FCSTD DOCUMENT  (FreeCAD 0.21R33694 (Git))
Label: lid_assembly
License: All rights reserved
LicenseURL: http://en.wikipedia.org/wiki/All_rights_reserved
objects: App::Link×9, App::Part×1
EXTERNAL_REF file=../master_kumiko_box.FCStd obj=Spreadsheet
EXTERNAL_REF file=../parts/box/kumiko_lid_long.FCStd obj=Body001
EXTERNAL_REF file=../parts/box/kumiko_lid_short.FCStd obj=Body001
EXTERNAL_REF file=../parts/box/kumiko_box_key_miter.FCStd obj=Body014

FEATURE [App::Link] Link  label="SpreadSheet"
  LinkedObject = -> <external ../master_kumiko_box.FCStd>#Spreadsheet
FEATURE [App::Link] Link001  label="lid_front"
  LinkPlacement = pos=(0,0,0) rot=(0,0,1;1.5708rad)
  LinkedObject = -> <external ../parts/box/kumiko_lid_long.FCStd>#Body001
  Placement = pos=(0,0,0) rot=(0,0,1;1.5708rad)
  expr: .Placement.Base.x = 0
FEATURE [App::Link] Link002  label="lid_left"
  LinkPlacement = pos=(0,75,0) rot=(0,0,1;0rad)
  LinkedObject = -> <external ../parts/box/kumiko_lid_short.FCStd>#Body001
  Placement = pos=(0,75,0) rot=(0,0,1;0rad)
  expr: .Placement.Base.y = <<SpreadSheet>>.box_width
FEATURE [App::Link] Link003  label="lid_back"
  LinkPlacement = pos=(130,75,0) rot=(0,0,1;4.71239rad)
  LinkedObject = -> <external ../parts/box/kumiko_lid_long.FCStd>#Body001
  Placement = pos=(130,75,0) rot=(0,0,1;4.71239rad)
  expr: .Placement.Base.x = <<SpreadSheet>>.box_length
  expr: .Placement.Base.y = <<SpreadSheet>>.box_width
FEATURE [App::Link] Link004  label="lid_side"
  LinkPlacement = pos=(130,0,0) rot=(0,0,1;3.14159rad)
  LinkedObject = -> <external ../parts/box/kumiko_lid_short.FCStd>#Body001
  Placement = pos=(130,0,0) rot=(0,0,1;3.14159rad)
  expr: .Placement.Base.x = <<SpreadSheet>>.box_length
  expr: .Placement.Rotation.Angle = 180
FEATURE [App::Link] Link005  label="miter_key_a"
  LinkPlacement = pos=(0,0,7) rot=(0,0,1;0rad)
  LinkedObject = -> <external ../parts/box/kumiko_box_key_miter.FCStd>#Body014
  Placement = pos=(0,0,7) rot=(0,0,1;0rad)
  expr: .Placement.Base.z = (<<SpreadSheet>>.lid_height - <<SpreadSheet>>.kumiko_thickness) / 2
FEATURE [App::Link] Link006  label="miter_key_b"
  LinkPlacement = pos=(130,0,7) rot=(0,0,1;1.5708rad)
  LinkedObject = -> <external ../parts/box/kumiko_box_key_miter.FCStd>#Body014
  Placement = pos=(130,0,7) rot=(0,0,1;1.5708rad)
  expr: .Placement.Base.x = <<SpreadSheet>>.box_length
  expr: .Placement.Base.z = (<<SpreadSheet>>.lid_height - <<SpreadSheet>>.kumiko_thickness) / 2
  expr: .Placement.Rotation.Angle = 90
FEATURE [App::Link] Link007  label="miter_key_c"
  LinkPlacement = pos=(130,75,7) rot=(0,0,1;3.14159rad)
  LinkedObject = -> <external ../parts/box/kumiko_box_key_miter.FCStd>#Body014
  Placement = pos=(130,75,7) rot=(0,0,1;3.14159rad)
  expr: .Placement.Base.x = <<SpreadSheet>>.box_length
  expr: .Placement.Base.y = <<SpreadSheet>>.box_width
  expr: .Placement.Base.z = (<<SpreadSheet>>.lid_height - <<SpreadSheet>>.kumiko_thickness) / 2
FEATURE [App::Link] Link008  label="miter_key_d"
  LinkPlacement = pos=(0,75,7) rot=(0,0,1;4.71239rad)
  LinkedObject = -> <external ../parts/box/kumiko_box_key_miter.FCStd>#Body014
  Placement = pos=(0,75,7) rot=(0,0,1;4.71239rad)
  expr: .Placement.Base.y = <<SpreadSheet>>.box_width
  expr: .Placement.Base.z = (<<SpreadSheet>>.lid_height - <<SpreadSheet>>.kumiko_thickness) / 2
  expr: .Placement.Rotation.Angle = 270
FEATURE [App::Part] Part  label="lid"
  Group = -> [Link004,Link003,Link002,Link001,Link005,Link006,Link007,Link008]
  Origin = -> Origin

RESOLVED EXTERNAL PARTS (link-assembly join: the EXTERNAL_REF files above that resolve inside this repo's crawl, each included once):
---- part ../master_kumiko_box.FCStd = doc fcstd_d57fc246fb5e ----
FCSTD DOCUMENT  (FreeCAD 0.21R33771 (Git))
Label: master_kumiko_box
License: All rights reserved
LicenseURL: https://en.wikipedia.org/wiki/All_rights_reserved
objects: App::Link×3, App::Part×2, Spreadsheet::Sheet×1
EXTERNAL_REF file=assembly/box_assembly.FCStd obj=Part
EXTERNAL_REF file=assembly/lid_assembly.FCStd obj=Part
EXTERNAL_REF file=assembly/kumiko_assembly.FCStd obj=Part001

FEATURE [Spreadsheet::Sheet] Spreadsheet  label="SpreadSheet"
  cells = A1='name; B1='value; C1='calc (y/n); A2='box_length; B2(box_length)=130; C2='n; A3='box_width; B3(box_width)==B2 / 2 + B5 - B13 / 2; C3='n; A4='box_height; B4(box_height)=60; C4='y; A5='box_thickness; B5(box_thickness)=11.5; C5='y; A7='lid_height; B7(lid_height)==B8 * 17 / 8.5; C7='y; A8='lid_frame_width; B8(lid_frame_width)==B5 - B13; C8='y; A9='lid_lip_width; B9(lid_lip_width)==B5 - B8; C9='y; A10='lid_lip_height; B10(lid_lip_hight)=3; C10='y; A12='kumiko_hight; B12(kumiko_hight)==B7 * 11 / 17; C12='y; A13='kumiko_thickness; B13(kumiko_thickness)=3; C13='n; A14='kumiko_grid_size; B14(kumiko_grid_size)==(B2 - 2 * B8 - B13) / 4; C14='y; A16='box_wall_height; B16(box_wall_height)==B4 - B7 - B18; C16='y; A18='floor_edge; B18(floor_edge)=2; C18='n; A20='cnc_spacing; B20(cnc_spacing)=0; C20='y
FEATURE [App::Link] Link  label="box"
  LinkedObject = -> <external assembly/box_assembly.FCStd>#Part
FEATURE [App::Link] Link001  label="lid"
  LinkPlacement = pos=(0,0,43) rot=(0,0,1;0rad)
  LinkedObject = -> <external assembly/lid_assembly.FCStd>#Part
  Placement = pos=(0,0,43) rot=(0,0,1;0rad)
  expr: .Placement.Base.z = <<SpreadSheet>>.box_height - <<SpreadSheet>>.lid_height
FEATURE [App::Link] Link002  label="kumiko_assembly"
  LinkPlacement = pos=(8.5,8.5,49) rot=(0,0,1;0rad)
  LinkedObject = -> <external assembly/kumiko_assembly.FCStd>#Part001
  Placement = pos=(8.5,8.5,49) rot=(0,0,1;0rad)
  expr: .Placement.Base.x = <<SpreadSheet>>.lid_frame_width
  expr: .Placement.Base.y = <<SpreadSheet>>.lid_frame_width
  expr: .Placement.Base.z = <<SpreadSheet>>.box_height - Spreadsheet.kumiko_hight
FEATURE [App::Part] Part  label="lid_complete"
  Group = -> [Link002,Link001]
  Origin = -> Origin
FEATURE [App::Part] Part001  label="kumiko_box_complete"
  Group = -> [Part,Link]
  Origin = -> Origin001
---- part ../parts/box/kumiko_box_key_miter.FCStd = doc fcstd_dc4a3549b709 ----
FCSTD DOCUMENT  (FreeCAD 0.21R33694 (Git))
Label: kumiko_box_key_miter
License: All rights reserved
LicenseURL: https://en.wikipedia.org/wiki/All_rights_reserved
objects: Sketcher::SketchObject×1, PartDesign::Pad×1, PartDesign::Body×1, App::Link×1
note: 4 computed .brp shape members not serialized (recipe doc carries the construction recipe); baked Part::Feature solids carry a one-line shape summary decoded from their .brp
EXTERNAL_REF file=../../master_kumiko_box.FCStd obj=Spreadsheet

FEATURE [Sketcher::SketchObject] Sketch027  label="miter_key_drawing"
  FullyConstrained = true
  MapMode = 5
  Support = -> [XY_Plane016]
  expr: Constraints[6] = <<SpreadSheet>>.lid_frame_width
  expr: Constraints[7] = 0
  expr: Constraints[8] = 0
  sketch-geometry (3):
    g0: LineSegment StartX=0 StartY=8.5 StartZ=0 EndX=0 EndY=0 EndZ=0
    g1: LineSegment StartX=0 StartY=0 StartZ=0 EndX=8.5 EndY=0 EndZ=0
    g2: LineSegment StartX=8.5 StartY=0 StartZ=0 EndX=0 EndY=8.5 EndZ=0
  constraints (9):
    c: Vertical(g0)
    c: Coincident(g1,g0)
    c: Horizontal(g1)
    c: Coincident(g2,g1)
    c: Coincident(g2,g0)
    c: Equal(g0,g1)
    c: DistanceX(g1,g1) = 8.5
    c: DistanceX(g-1,g0) = 0
    c: DistanceY(g0,g-1) = 0
FEATURE [PartDesign::Pad] Pad012  label="miter_key_extrude"
  Direction = (0,0,1)
  Length = 3
  Length2 = 10
  Profile = -> Sketch027
  ReferenceAxis = -> Sketch027 [N_Axis]
  Type = 0
  expr: Length = <<SpreadSheet>>.kumiko_thickness
FEATURE [PartDesign::Body] Body014  label="miter_key"
  Group = -> [Sketch027,Pad012]
  Origin = -> Origin016
  Tip = -> Pad012
  expr: .Placement.Base.x = 0
  expr: .Placement.Base.y = 0
  expr: .Placement.Base.z = 0
  expr: .Placement.Rotation.Angle = 0
  expr: .Placement.Rotation.Axis.x = 0
  expr: .Placement.Rotation.Axis.y = 0
  expr: .Placement.Rotation.Axis.z = 1
FEATURE [App::Link] Link  label="SpreadSheet"
  LinkedObject = -> <external ../../master_kumiko_box.FCStd>#Spreadsheet
---- part ../parts/box/kumiko_lid_long.FCStd = doc fcstd_c46aa1aee5ec ----
FCSTD DOCUMENT  (FreeCAD 0.21R33694 (Git))
Label: kumiko_lid_long
License: All rights reserved
LicenseURL: https://en.wikipedia.org/wiki/All_rights_reserved
objects: Sketcher::SketchObject×3, PartDesign::Pocket×2, PartDesign::Pad×1, PartDesign::Mirrored×1, PartDesign::Body×1, App::Link×1
note: 11 computed .brp shape members not serialized (recipe doc carries the construction recipe); baked Part::Feature solids carry a one-line shape summary decoded from their .brp
EXTERNAL_REF file=../../master_kumiko_box.FCStd obj=Spreadsheet

FEATURE [Sketcher::SketchObject] Sketch004  label="lid_profile_drawing"
  FullyConstrained = true
  MapMode = 5
  Placement = pos=(0,0,0) rot=(1,0,0;1.5708rad)
  Support = -> [XZ_Plane001]
  expr: Constraints[18] = <<SpreadSheet>>.lid_height
  expr: Constraints[19] = <<SpreadSheet>>.kumiko_hight
  expr: Constraints[20] = <<SpreadSheet>>.lid_lip_hight
  expr: Constraints[21] = <<SpreadSheet>>.lid_frame_width
  expr: Constraints[22] = <<SpreadSheet>>.box_thickness / 2
  expr: Constraints[23] = <<SpreadSheet>>.box_thickness
  sketch-geometry (8):
    g0: LineSegment StartX=0 StartY=0 StartZ=0 EndX=0 EndY=17 EndZ=0
    g1: LineSegment StartX=0 StartY=17 StartZ=0 EndX=8.5 EndY=17 EndZ=0
    g2: LineSegment StartX=8.5 StartY=17 StartZ=0 EndX=8.5 EndY=6 EndZ=0
    g3: LineSegment StartX=8.5 StartY=6 StartZ=0 EndX=11.5 EndY=6 EndZ=0
    g4: LineSegment StartX=11.5 StartY=6 StartZ=0 EndX=11.5 EndY=3 EndZ=0
    g5: LineSegment StartX=11.5 StartY=3 StartZ=0 EndX=5.75 EndY=3 EndZ=0
    g6: LineSegment StartX=5.75 StartY=3 StartZ=0 EndX=5.75 EndY=0 EndZ=0
    g7: LineSegment StartX=5.75 StartY=0 StartZ=0 EndX=0 EndY=0 EndZ=0
  constraints (24):
    c: Vertical(g0)
    c: Coincident(g1,g0)
    c: Horizontal(g1)
    c: Coincident(g2,g1)
    c: Vertical(g2)
    c: Coincident(g3,g2)
    c: Horizontal(g3)
    c: Coincident(g4,g3)
    c: Vertical(g4)
    c: Coincident(g5,g4)
    c: Horizontal(g5)
    c: Coincident(g6,g5)
    c: Vertical(g6)
    c: Coincident(g7,g6)
    c: Coincident(g7,g0)
    c: Horizontal(g7)
    c: DistanceX(g-1,g0) = 0
    c: DistanceY(g-1,g0) = 0
    c: DistanceY(g0,g0) = 17
    c: DistanceY(g2,g2) = 11
    c: DistanceY(g4,g4) = 3
    c: DistanceX(g1,g1) = 8.5
    c: DistanceX(g5,g5) = 5.75
    c: DistanceX(g0,g3) = 11.5
FEATURE [PartDesign::Pad] Pad001  label="lid_extrusion"
  Direction = (0,-1,-2e-16)
  Length = 65
  Length2 = 10
  Placement = pos=(0,0,0) rot=(1,0,0;1.5708rad)
  Profile = -> Sketch004
  ReferenceAxis = -> Sketch004 [N_Axis]
  Type = 0
  expr: Length = <<SpreadSheet>>.box_length / 2
FEATURE [Sketcher::SketchObject] Sketch005  label="miter_drawing"
  FullyConstrained = true
  MapMode = 5
  Placement = pos=(0,0,0) rot=(1,0,0;3.14159rad)
  Support = -> [Pad001]
  expr: Constraints[6] = <<SpreadSheet>>.box_thickness
  expr: Constraints[8] = <<SpreadSheet>>.box_thickness
  sketch-geometry (3):
    g0: LineSegment StartX=0 StartY=0 StartZ=0 EndX=11.5 EndY=0 EndZ=0
    g1: LineSegment StartX=11.5 StartY=0 StartZ=0 EndX=11.5 EndY=11.5 EndZ=0
    g2: LineSegment StartX=11.5 StartY=11.5 StartZ=0 EndX=0 EndY=0 EndZ=0
  constraints (9):
    c: Horizontal(g0)
    c: Coincident(g1,g0)
    c: Vertical(g1)
    c: Coincident(g2,g1)
    c: Coincident(g2,g0)
    c: DistanceX(g-1,g0) = 0
    c: DistanceX(g-1,g0) = 11.5
    c: DistanceY(g0,g-1) = 0
    c: DistanceY(g0,g1) = 11.5
FEATURE [PartDesign::Pocket] Pocket002  label="miter_cut"
  BaseFeature = -> Pad001
  Direction = (0,-2e-16,1)
  Length = 17
  Length2 = 5
  Placement = pos=(0,0,0) rot=(1,0,0;1.5708rad)
  Profile = -> Sketch005
  ReferenceAxis = -> Sketch005 [N_Axis]
  Type = 0
  expr: Length = <<SpreadSheet>>.lid_height
FEATURE [Sketcher::SketchObject] Sketch006  label="miter_key_drawing"
  FullyConstrained = true
  MapMode = 5
  Placement = pos=(0,0,0) rot=(0.678598,0.281085,0.678598;3.68962rad)
  Support = -> [Pocket002]
  expr: Constraints[10] = <<SpreadSheet>>.kumiko_thickness
  expr: Constraints[11] = <<SpreadSheet>>.lid_frame_width * sqrt(2) / 2
  expr: Constraints[9] = (<<SpreadSheet>>.lid_height - <<SpreadSheet>>.kumiko_thickness) / 2
  sketch-geometry (4):
    g0: LineSegment StartX=7 StartY=6.01041 StartZ=0 EndX=10 EndY=6.01041 EndZ=0
    g1: LineSegment StartX=10 StartY=6.01041 StartZ=0 EndX=10 EndY=0 EndZ=0
    g2: LineSegment StartX=10 StartY=0 StartZ=0 EndX=7 EndY=0 EndZ=0
    g3: LineSegment StartX=7 StartY=0 StartZ=0 EndX=7 EndY=6.01041 EndZ=0
  constraints (12):
    c: Coincident(g0,g1)
    c: Coincident(g1,g2)
    c: Coincident(g2,g3)
    c: Coincident(g3,g0)
    c: Horizontal(g0)
    c: Horizontal(g2)
    c: Vertical(g1)
    c: Vertical(g3)
    c: PointOnObject(g1,g-1)
    c: DistanceX(g-1,g2) = 7
    c: DistanceX(g0,g0) = 3
    c: DistanceY(g-1,g0) = 6.01041
FEATURE [PartDesign::Pocket] Pocket003  label="miter_key_cut"
  BaseFeature = -> Pocket002
  Direction = (-0.707107,-0.707107,-1e-16)
  Length = 4
  Length2 = 5
  Placement = pos=(0,0,0) rot=(1,0,0;1.5708rad)
  Profile = -> Sketch006
  ReferenceAxis = -> Sketch006 [N_Axis]
  Type = 1
FEATURE [PartDesign::Mirrored] Mirrored001  label="lid_long_mirror"
  BaseFeature = -> Pocket003
  MirrorPlane = -> Pocket003 [Face7]
  Originals = -> [Pad001,Pocket002,Pocket003]
  Placement = pos=(0,0,0) rot=(1,0,0;1.5708rad)
  Refine = true
FEATURE [PartDesign::Body] Body001  label="lid_long_body"
  Group = -> [Sketch004,Pad001,Sketch005,Pocket002,Sketch006,Pocket003,Mirrored001]
  Origin = -> Origin001
  Tip = -> Mirrored001
  expr: .Placement.Base.x = 0
  expr: .Placement.Base.y = 0
  expr: .Placement.Base.z = 0
  expr: .Placement.Rotation.Angle = 0
  expr: .Placement.Rotation.Axis.x = 0
  expr: .Placement.Rotation.Axis.y = 0
  expr: .Placement.Rotation.Axis.z = 1
FEATURE [App::Link] Link  label="SpreadSheet"
  LinkedObject = -> <external ../../master_kumiko_box.FCStd>#Spreadsheet
---- part ../parts/box/kumiko_lid_short.FCStd = doc fcstd_e5b578333dee ----
FCSTD DOCUMENT  (FreeCAD 0.21R33694 (Git))
Label: kumiko_lid_short
License: All rights reserved
LicenseURL: https://en.wikipedia.org/wiki/All_rights_reserved
objects: Sketcher::SketchObject×3, PartDesign::Pocket×2, PartDesign::Pad×1, PartDesign::Mirrored×1, PartDesign::Body×1, App::Link×1
note: 11 computed .brp shape members not serialized (recipe doc carries the construction recipe); baked Part::Feature solids carry a one-line shape summary decoded from their .brp
EXTERNAL_REF file=../../master_kumiko_box.FCStd obj=Spreadsheet

FEATURE [Sketcher::SketchObject] Sketch004  label="lid_profile_drawing"
  FullyConstrained = true
  MapMode = 5
  Placement = pos=(0,0,0) rot=(1,0,0;1.5708rad)
  Support = -> [XZ_Plane001]
  expr: Constraints[18] = <<SpreadSheet>>.lid_height
  expr: Constraints[19] = <<SpreadSheet>>.kumiko_hight
  expr: Constraints[20] = <<SpreadSheet>>.lid_lip_hight
  expr: Constraints[21] = <<SpreadSheet>>.lid_frame_width
  expr: Constraints[22] = <<SpreadSheet>>.box_thickness / 2
  expr: Constraints[23] = <<SpreadSheet>>.box_thickness
  sketch-geometry (8):
    g0: LineSegment StartX=0 StartY=0 StartZ=0 EndX=0 EndY=17 EndZ=0
    g1: LineSegment StartX=0 StartY=17 StartZ=0 EndX=8.5 EndY=17 EndZ=0
    g2: LineSegment StartX=8.5 StartY=17 StartZ=0 EndX=8.5 EndY=6 EndZ=0
    g3: LineSegment StartX=8.5 StartY=6 StartZ=0 EndX=11.5 EndY=6 EndZ=0
    g4: LineSegment StartX=11.5 StartY=6 StartZ=0 EndX=11.5 EndY=3 EndZ=0
    g5: LineSegment StartX=11.5 StartY=3 StartZ=0 EndX=5.75 EndY=3 EndZ=0
    g6: LineSegment StartX=5.75 StartY=3 StartZ=0 EndX=5.75 EndY=0 EndZ=0
    g7: LineSegment StartX=5.75 StartY=0 StartZ=0 EndX=0 EndY=0 EndZ=0
  constraints (24):
    c: Vertical(g0)
    c: Coincident(g1,g0)
    c: Horizontal(g1)
    c: Coincident(g2,g1)
    c: Vertical(g2)
    c: Coincident(g3,g2)
    c: Horizontal(g3)
    c: Coincident(g4,g3)
    c: Vertical(g4)
    c: Coincident(g5,g4)
    c: Horizontal(g5)
    c: Coincident(g6,g5)
    c: Vertical(g6)
    c: Coincident(g7,g6)
    c: Coincident(g7,g0)
    c: Horizontal(g7)
    c: DistanceX(g-1,g0) = 0
    c: DistanceY(g-1,g0) = 0
    c: DistanceY(g0,g0) = 17
    c: DistanceY(g2,g2) = 11
    c: DistanceY(g4,g4) = 3
    c: DistanceX(g1,g1) = 8.5
    c: DistanceX(g5,g5) = 5.75
    c: DistanceX(g0,g3) = 11.5
FEATURE [PartDesign::Pad] Pad001  label="lid_extrusion"
  Direction = (0,-1,-2e-16)
  Length = 37.5
  Length2 = 10
  Placement = pos=(0,0,0) rot=(1,0,0;1.5708rad)
  Profile = -> Sketch004
  ReferenceAxis = -> Sketch004 [N_Axis]
  Type = 0
  expr: Length = <<SpreadSheet>>.box_width / 2
FEATURE [Sketcher::SketchObject] Sketch005  label="miter_drawing"
  FullyConstrained = true
  MapMode = 5
  Placement = pos=(0,0,0) rot=(1,0,0;3.14159rad)
  Support = -> [Pad001]
  expr: Constraints[6] = <<SpreadSheet>>.box_thickness
  expr: Constraints[8] = <<SpreadSheet>>.box_thickness
  sketch-geometry (3):
    g0: LineSegment StartX=0 StartY=0 StartZ=0 EndX=11.5 EndY=0 EndZ=0
    g1: LineSegment StartX=11.5 StartY=0 StartZ=0 EndX=11.5 EndY=11.5 EndZ=0
    g2: LineSegment StartX=11.5 StartY=11.5 StartZ=0 EndX=0 EndY=0 EndZ=0
  constraints (9):
    c: Horizontal(g0)
    c: Coincident(g1,g0)
    c: Vertical(g1)
    c: Coincident(g2,g1)
    c: Coincident(g2,g0)
    c: DistanceX(g-1,g0) = 0
    c: DistanceX(g-1,g0) = 11.5
    c: DistanceY(g0,g-1) = 0
    c: DistanceY(g0,g1) = 11.5
FEATURE [PartDesign::Pocket] Pocket002  label="miter_cut"
  BaseFeature = -> Pad001
  Direction = (0,-2e-16,1)
  Length = 17
  Length2 = 5
  Placement = pos=(0,0,0) rot=(1,0,0;1.5708rad)
  Profile = -> Sketch005
  ReferenceAxis = -> Sketch005 [N_Axis]
  Type = 0
  expr: Length = <<SpreadSheet>>.lid_height
FEATURE [Sketcher::SketchObject] Sketch006  label="miter_key_drawing"
  FullyConstrained = true
  MapMode = 5
  Placement = pos=(0,0,0) rot=(0.678598,0.281085,0.678598;3.68962rad)
  Support = -> [Pocket002]
  expr: Constraints[10] = <<SpreadSheet>>.kumiko_thickness
  expr: Constraints[11] = <<SpreadSheet>>.lid_frame_width * sqrt(2) / 2
  expr: Constraints[9] = (<<SpreadSheet>>.lid_height - <<SpreadSheet>>.kumiko_thickness) / 2
  sketch-geometry (4):
    g0: LineSegment StartX=7 StartY=6.01041 StartZ=0 EndX=10 EndY=6.01041 EndZ=0
    g1: LineSegment StartX=10 StartY=6.01041 StartZ=0 EndX=10 EndY=0 EndZ=0
    g2: LineSegment StartX=10 StartY=0 StartZ=0 EndX=7 EndY=0 EndZ=0
    g3: LineSegment StartX=7 StartY=0 StartZ=0 EndX=7 EndY=6.01041 EndZ=0
  constraints (12):
    c: Coincident(g0,g1)
    c: Coincident(g1,g2)
    c: Coincident(g2,g3)
    c: Coincident(g3,g0)
    c: Horizontal(g0)
    c: Horizontal(g2)
    c: Vertical(g1)
    c: Vertical(g3)
    c: PointOnObject(g1,g-1)
    c: DistanceX(g-1,g2) = 7
    c: DistanceX(g0,g0) = 3
    c: DistanceY(g-1,g0) = 6.01041
FEATURE [PartDesign::Pocket] Pocket003  label="miter_key_cut"
  BaseFeature = -> Pocket002
  Direction = (-0.707107,-0.707107,-1e-16)
  Length = 4
  Length2 = 5
  Placement = pos=(0,0,0) rot=(1,0,0;1.5708rad)
  Profile = -> Sketch006
  ReferenceAxis = -> Sketch006 [N_Axis]
  Type = 1
FEATURE [PartDesign::Mirrored] Mirrored001  label="lid_mirror"
  BaseFeature = -> Pocket003
  MirrorPlane = -> Pocket003 [Face7]
  Originals = -> [Pad001,Pocket002,Pocket003]
  Placement = pos=(0,0,0) rot=(1,0,0;1.5708rad)
  Refine = true
FEATURE [PartDesign::Body] Body001  label="lid_side"
  Group = -> [Sketch004,Pad001,Sketch005,Pocket002,Sketch006,Pocket003,Mirrored001]
  Origin = -> Origin001
  Tip = -> Mirrored001
  expr: .Placement.Base.x = 0
  expr: .Placement.Base.y = 0
  expr: .Placement.Base.z = 0
  expr: .Placement.Rotation.Angle = 0
  expr: .Placement.Rotation.Axis.x = 0
  expr: .Placement.Rotation.Axis.y = 0
  expr: .Placement.Rotation.Axis.z = 1
FEATURE [App::Link] Link  label="SpreadSheet"
  LinkedObject = -> <external ../../master_kumiko_box.FCStd>#Spreadsheet
